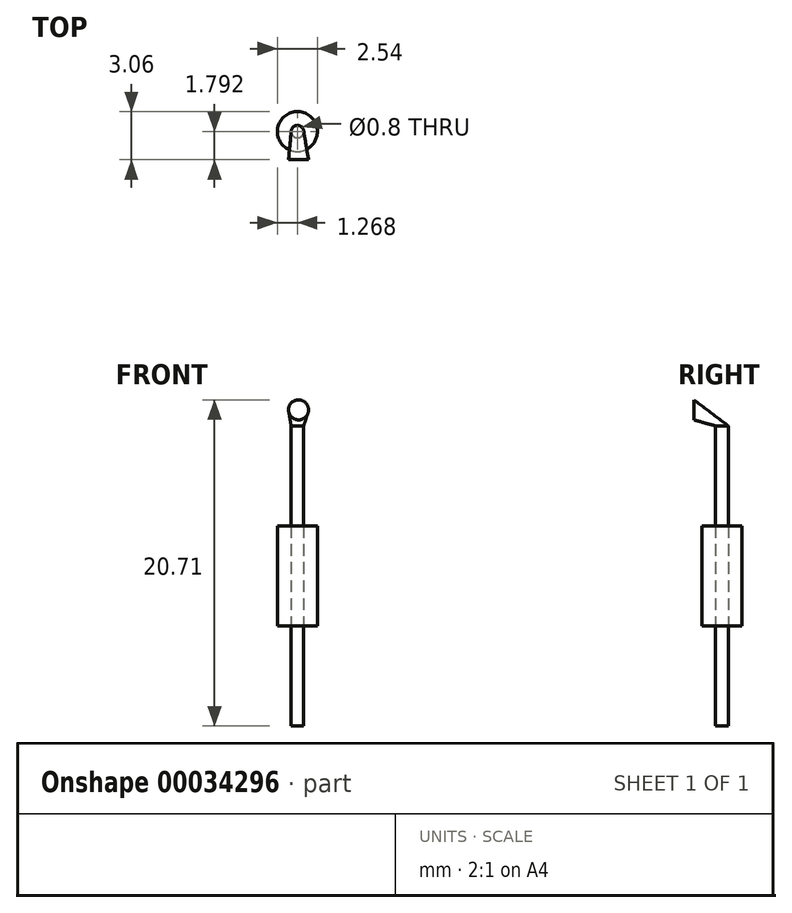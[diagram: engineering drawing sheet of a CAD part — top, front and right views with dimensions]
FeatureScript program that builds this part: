
annotation { "Feature Type Name" : "Feature", "Feature Type Description" : "" }
export const myFeature = defineFeature(function(context is Context, id is Id, definition is map)
    precondition{}
    {
        {
            var Q0;
            Q0=qCreatedBy(makeId("Top.planeOp"),FACE);
            var sketch = newSketch(context, id + "F0", { "sketchPlane" : qUnion([Q0])});
            skCircle(sketch, "E0", {"center": v(19.73, 19.57) * mm, "radius": 1.27 * mm});
            skCircle(sketch, "E1", {"center": v(19.73, 19.57) * mm, "radius": 0.4 * mm});
            skSolve(sketch);
        }
        {
            var Q0;
            Q0=makeQuery(id+"F0.imprint","IMPRINT",FACE,{"disambiguationData":[TD([[makeQuery(id+"F0.imprint","IMPRINT",EDGE,{"derivedFrom":sQuery(id+"F0.wireOp",EDGE,"E0")}),1.0]])]});
            extrude(context, id + "F1", {"entities" : qUnion([Q0]), "endBound" : BoundingType.SYMMETRIC, "oppositeDirection" : true, "depth" : 6.35 * mm});
        }
        {
            var Q0;
            Q0=makeQuery(id+"F0.imprint","IMPRINT",FACE,{"disambiguationData":[TD([[makeQuery(id+"F0.imprint","IMPRINT",EDGE,{"derivedFrom":sQuery(id+"F0.wireOp",EDGE,"E1")}),1.0]])]});
            extrude(context, id + "F2", {"entities" : qUnion([Q0]), "endBound" : BoundingType.SYMMETRIC, "depth" : 19.05 * mm});
        }
        {
            var Q0;
            Q0=qCreatedBy(makeId("Front.planeOp"),FACE);
            cPlane(context, id + "F3", {"entities" : qUnion([Q0]), "cplaneType" : CPlaneType.OFFSET, "offset" : 17.78 * mm, "oppositeDirection" : true, "width" : 152.4 * mm, "height" : 152.4 * mm});
        }
        {
            var Q0;
            Q0=qCreatedBy(id+"F3.planeOp",FACE);
            var sketch = newSketch(context, id + "F4", { "sketchPlane" : qUnion([Q0])});
            skCircle(sketch, "E2", {"center": v(19.8, 10.54) * mm, "radius": 0.63 * mm});
            skSolve(sketch);
        }
        {
            var Q0;
            Q0=makeQuery(id+"F4.imprint","IMPRINT",FACE,{"disambiguationData":[TD([[makeQuery(id+"F4.imprint","IMPRINT",EDGE,{"derivedFrom":sQuery(id+"F4.wireOp",EDGE,"E2")}),1.0]])]});
            var Q1;
            Q1=makeQuery(id+"F2.opExtrude","CAP_FACE",FACE,{"disambiguationData":[OSD([sQuery(id+"F0.wireOp",EDGE,"E1")])],"isStart":false});
            loft(context, id + "F5", {"sheetProfilesArray" : [{ "sheetProfileEntities" : qUnion([Q0]) }, { "sheetProfileEntities" : qUnion([Q1]) }]});
        }
    });
